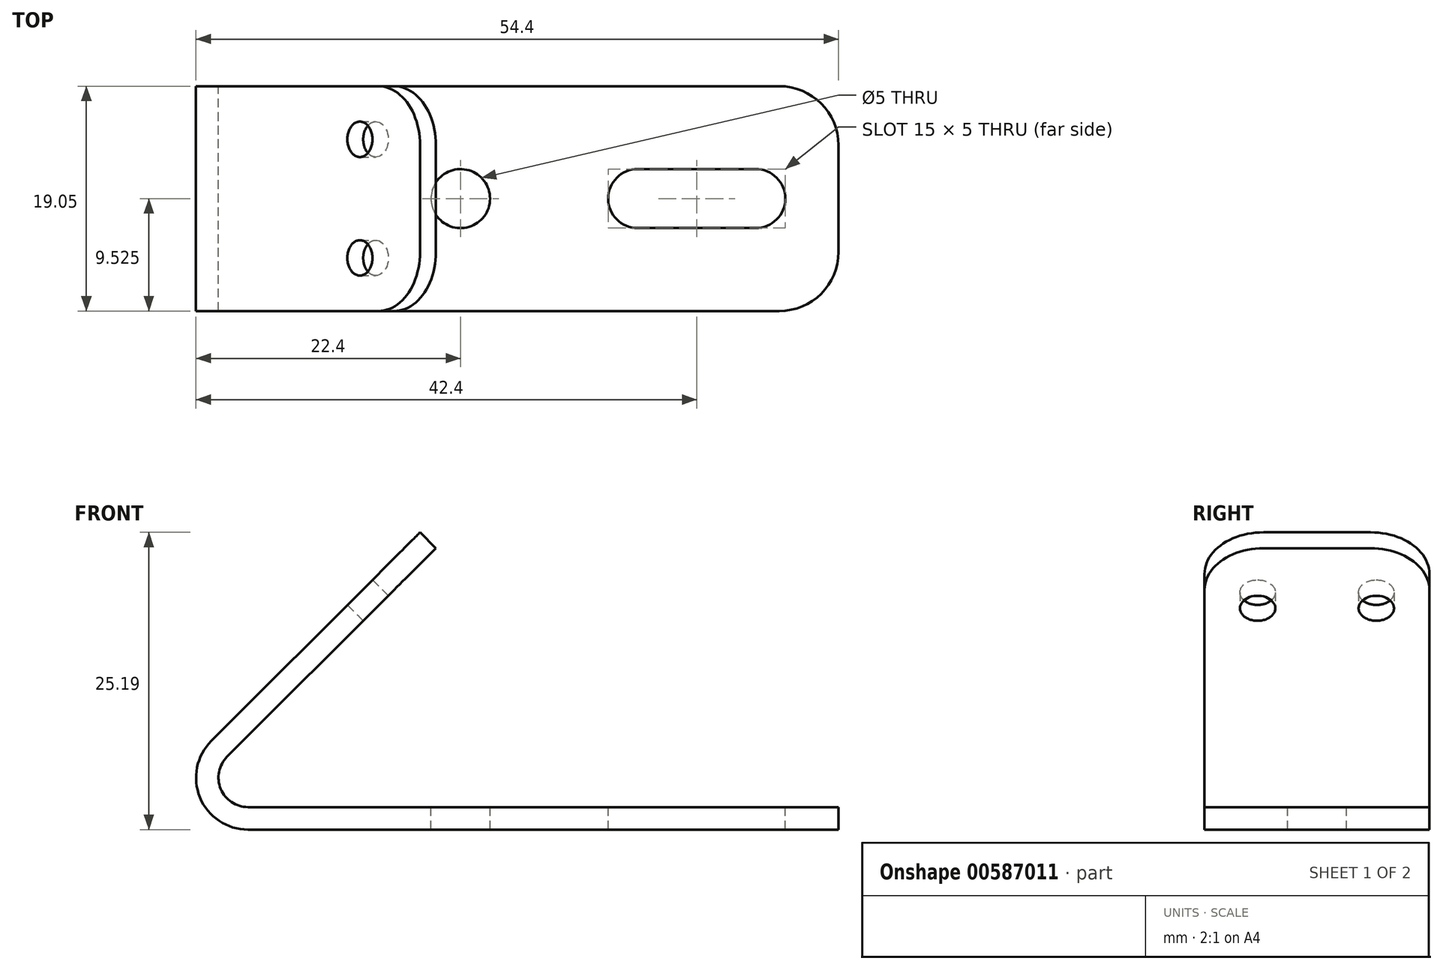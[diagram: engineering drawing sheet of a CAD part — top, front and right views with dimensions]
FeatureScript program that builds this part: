
annotation { "Feature Type Name" : "Feature", "Feature Type Description" : "" }
export const myFeature = defineFeature(function(context is Context, id is Id, definition is map)
    precondition{}
    {
        {
            var Q0;
            Q0=qCreatedBy(makeId("Front.planeOp"),FACE);
            var sketch = newSketch(context, id + "F0", { "sketchPlane" : qUnion([Q0])});
            skLineSegment(sketch, "E0", {"start": v(0, 0) * mm, "end": v(50, 0) * mm});
            skLineSegment(sketch, "E1", {"start": v(50, 0) * mm, "end": v(50, 1.9) * mm});
            skLineSegment(sketch, "E2", {"start": v(50, 1.9) * mm, "end": v(0, 1.9) * mm});
            skLineSegment(sketch, "E3", {"start": v(0, 1.9) * mm, "end": v(0, 0) * mm});
            skPoint(sketch, "E4", {"position": v(0, 4.4) * mm});
            skArc(sketch, "E5", {"start": v(0, 0) * mm, "mid": v(-4.4, 4.4) * mm, "end": v(0, 8.8) * mm});
            skArc(sketch, "E6", {"start": v(0, 1.9) * mm, "mid": v(-2.5, 4.4) * mm, "end": v(0, 6.9) * mm});
            skLineSegment(sketch, "E7", {"start": v(-3.11, 7.51) * mm, "end": v(14.57, 25.19) * mm});
            skLineSegment(sketch, "E8", {"start": v(14.57, 25.19) * mm, "end": v(15.9, 23.85) * mm});
            skLineSegment(sketch, "E9", {"start": v(15.9, 23.85) * mm, "end": v(-1.77, 6.17) * mm});
            skSolve(sketch);
        }
        {
            var Q0;
            Q0 = qSketchRegion(id + "F0", true);
            extrude(context, id + "F1", {"entities" : qUnion([Q0]), "depth" : 19.05 * mm, "offsetDistance" : 25 * mm});
        }
        {
            var Q0;
            Q0=makeQuery(id+"F1.opExtrude","SWEPT_FACE",FACE,{"disambiguationData":[OSD([sQuery(id+"F0.wireOp",EDGE,"E2")])]});
            var sketch = newSketch(context, id + "F2", { "sketchPlane" : qUnion([Q0])});
            skPoint(sketch, "E10", {"position": v(18, -9.53) * mm});
            skLineSegment(sketch, "E11", {"start": v(18, -9.53) * mm, "end": v(18, 0) * mm, "construction": true});
            skLineSegment(sketch, "E12", {"start": v(18, 0) * mm, "end": v(18, -19.05) * mm, "construction": true});
            skLineSegment(sketch, "E13", {"start": v(18, -9.53) * mm, "end": v(50, -9.53) * mm, "construction": true});
            skPoint(sketch, "E14", {"position": v(43, -9.53) * mm});
            skArc(sketch, "E15", {"start": v(43, -12.03) * mm, "mid": v(45.5, -9.53) * mm, "end": v(43, -7.03) * mm});
            skPoint(sketch, "E16", {"position": v(33, -9.53) * mm});
            skArc(sketch, "E17", {"start": v(33, -7.03) * mm, "mid": v(30.5, -9.53) * mm, "end": v(33, -12.03) * mm});
            skLineSegment(sketch, "E18", {"start": v(33, -7.03) * mm, "end": v(43, -7.03) * mm});
            skLineSegment(sketch, "E19", {"start": v(33, -12.03) * mm, "end": v(43, -12.03) * mm});
            skSolve(sketch);
        }
        {
            var Q0;
            Q0=makeQuery(id+"F2.imprint","IMPRINT",FACE,{"disambiguationData":[TD([[makeQuery(id+"F2.imprint","IMPRINT",EDGE,{"derivedFrom":sQuery(id+"F2.wireOp",EDGE,"E15")}),1.0]])]});
            extrude(context, id + "F3", {"entities" : qUnion([Q0]), "operationType" : NewBodyOperationType.REMOVE, "endBound" : BoundingType.THROUGH_ALL, "oppositeDirection" : true, "depth" : 25 * mm, "offsetDistance" : 25 * mm});
        }
        {
            var Q0;
            Q0=sQuery(id+"F2.wireOp",VERTEX,"E10");
            var Q1;
            Q1=makeQuery(id+"F1.opExtrude","SWEPT_BODY",BODY,{"disambiguationData":[OSD([sQuery(id+"F0.wireOp",EDGE,"E0"),sQuery(id+"F0.wireOp",EDGE,"E1"),sQuery(id+"F0.wireOp",EDGE,"E2"),sQuery(id+"F0.wireOp",EDGE,"E5"),sQuery(id+"F0.wireOp",EDGE,"E6"),sQuery(id+"F0.wireOp",EDGE,"E7"),sQuery(id+"F0.wireOp",EDGE,"E8"),sQuery(id+"F0.wireOp",EDGE,"E9")])]});
            hole(context, id + "F4", {"style" : HoleStyle.SIMPLE, "endStyle" : HoleEndStyle.THROUGH, "holeDiameter" : 5 * mm, "majorDiameter" : 5 * mm, "isTappedThrough" : true, "tappedDepth" : 12 * mm, "tapClearance" : 3, "startFromSketch" : true, "locations" : qUnion([Q0]), "scope" : qUnion([Q1])});
        }
        {
            var Q0;
            Q0=makeQuery(id+"F1.opExtrude","SWEPT_FACE",FACE,{"disambiguationData":[OSD([sQuery(id+"F0.wireOp",EDGE,"E9")])]});
            var sketch = newSketch(context, id + "F5", { "sketchPlane" : qUnion([Q0])});
            skPoint(sketch, "E20", {"position": v(-14.55, 20.91) * mm});
            skPoint(sketch, "E21", {"position": v(-4.5, 20.91) * mm});
            skCircle(sketch, "E22", {"center": v(-14.55, 20.91) * mm, "radius": 1.5 * mm});
            skCircle(sketch, "E23", {"center": v(-4.5, 20.91) * mm, "radius": 1.5 * mm});
            skSolve(sketch);
        }
        {
            var Q0;
            Q0=makeQuery(id+"F5.imprint","IMPRINT",FACE,{"disambiguationData":[TD([[makeQuery(id+"F5.imprint","IMPRINT",EDGE,{"derivedFrom":sQuery(id+"F5.wireOp",EDGE,"E22")}),1.0]])]});
            var Q1;
            Q1=makeQuery(id+"F5.imprint","IMPRINT",FACE,{"disambiguationData":[TD([[makeQuery(id+"F5.imprint","IMPRINT",EDGE,{"derivedFrom":sQuery(id+"F5.wireOp",EDGE,"E23")}),1.0]])]});
            extrude(context, id + "F6", {"entities" : qUnion([Q0, Q1]), "operationType" : NewBodyOperationType.REMOVE, "endBound" : BoundingType.THROUGH_ALL, "oppositeDirection" : true, "depth" : 25 * mm, "offsetDistance" : 25 * mm});
        }
        {
            var Q0;
            Q0=makeQuery(id+"F1.opExtrude","CAP_EDGE",EDGE,{"disambiguationData":[OSD([sQuery(id+"F0.wireOp",EDGE,"E1")])],"isStart":true});
            var Q1;
            Q1=makeQuery(id+"F1.opExtrude","CAP_EDGE",EDGE,{"disambiguationData":[OSD([sQuery(id+"F0.wireOp",EDGE,"E1")])],"isStart":false});
            var Q2;
            Q2=makeQuery(id+"F1.opExtrude","CAP_EDGE",EDGE,{"disambiguationData":[OSD([sQuery(id+"F0.wireOp",EDGE,"E8")])],"isStart":false});
            var Q3;
            Q3=makeQuery(id+"F1.opExtrude","CAP_EDGE",EDGE,{"disambiguationData":[OSD([sQuery(id+"F0.wireOp",EDGE,"E8")])],"isStart":true});
            fillet(context, id + "F7", {"entities" : qUnion([Q0, Q1, Q2, Q3]), "radius" : 5 * mm, "tangentPropagation" : true, "allowEdgeOverflow" : false});
        }
    });
